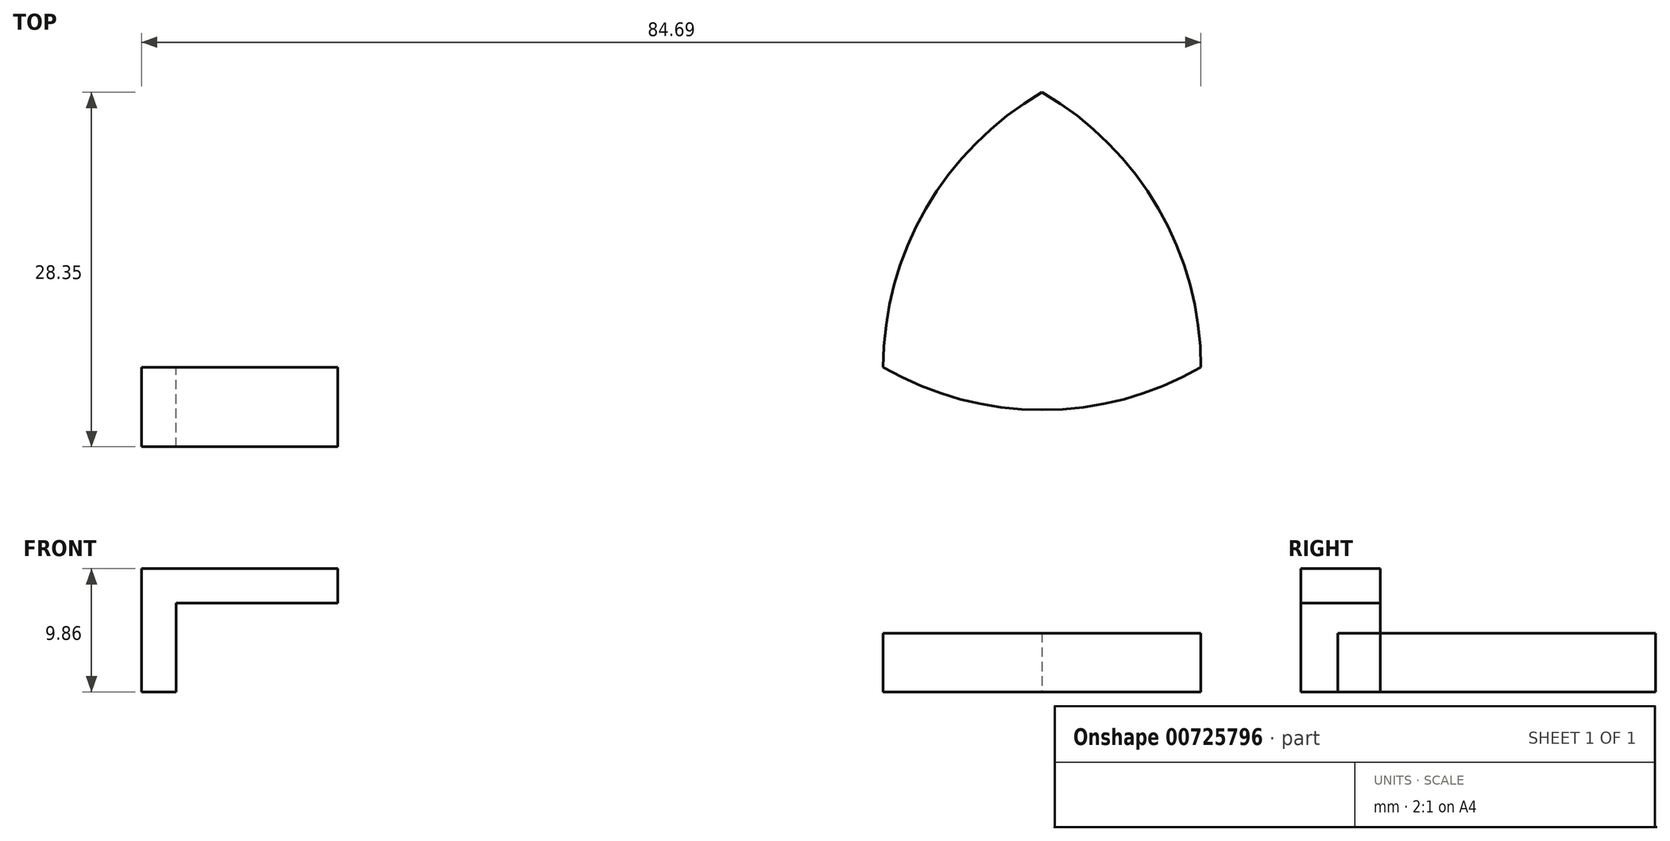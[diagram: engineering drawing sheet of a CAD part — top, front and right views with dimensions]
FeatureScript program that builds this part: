
annotation { "Feature Type Name" : "Feature", "Feature Type Description" : "" }
export const myFeature = defineFeature(function(context is Context, id is Id, definition is map)
    precondition{}
    {
        {
            var Q0;
            Q0=qCreatedBy(makeId("Top.planeOp"),FACE);
            var sketch = newSketch(context, id + "F0", { "sketchPlane" : qUnion([Q0])});
            skArc(sketch, "E0", {"start": v(-12.7, 0) * mm, "mid": v(0, -3.4) * mm, "end": v(12.7, 0) * mm});
            skArc(sketch, "E1", {"start": v(0, 22) * mm, "mid": v(-9.3, 12.7) * mm, "end": v(-12.7, 0) * mm});
            skArc(sketch, "E2", {"start": v(12.7, 0) * mm, "mid": v(9.3, 12.7) * mm, "end": v(0, 22) * mm});
            skPoint(sketch, "E3.end.orphan", {"position": v(6.35, 11) * mm});
            skPoint(sketch, "E4.end.orphan", {"position": v(-6.35, 11) * mm});
            skSolve(sketch);
        }
        {
            var Q0;
            Q0 = qSketchRegion(id + "F0", true);
            extrude(context, id + "F1", {"entities" : qUnion([Q0]), "depth" : 4.7 * mm, "offsetDistance" : 25.4 * mm});
        }
        {
            var Q0;
            Q0=qCreatedBy(makeId("Front.planeOp"),FACE);
            var sketch = newSketch(context, id + "F2", { "sketchPlane" : qUnion([Q0])});
            skLineSegment(sketch, "E5.bottom", {"start": v(-72, 0) * mm, "end": v(-69.23, 0) * mm});
            skLineSegment(sketch, "E5.top", {"start": v(-72, 7.1) * mm, "end": v(-69.23, 7.1) * mm});
            skLineSegment(sketch, "E5.left", {"start": v(-72, 0) * mm, "end": v(-72, 7.1) * mm});
            skLineSegment(sketch, "E5.right", {"start": v(-69.23, 0) * mm, "end": v(-69.23, 7.1) * mm});
            skLineSegment(sketch, "E6.bottom", {"start": v(-72, 7.1) * mm, "end": v(-56.32, 7.1) * mm});
            skLineSegment(sketch, "E6.top", {"start": v(-72, 9.86) * mm, "end": v(-56.32, 9.86) * mm});
            skLineSegment(sketch, "E6.left", {"start": v(-72, 7.1) * mm, "end": v(-72, 9.86) * mm});
            skLineSegment(sketch, "E6.right", {"start": v(-56.32, 7.1) * mm, "end": v(-56.32, 9.86) * mm});
            skLineSegment(sketch, "E7.bottom", {"start": v(-56.32, 7.1) * mm, "end": v(-58.72, 7.1) * mm});
            skLineSegment(sketch, "E7.top", {"start": v(-56.32, 0) * mm, "end": v(-58.72, 0) * mm});
            skLineSegment(sketch, "E7.left", {"start": v(-56.32, 7.1) * mm, "end": v(-56.32, 0) * mm});
            skLineSegment(sketch, "E7.right", {"start": v(-58.72, 7.1) * mm, "end": v(-58.72, 0) * mm});
            skSolve(sketch);
        }
        {
            var Q0;
            Q0=makeQuery(id+"F2.imprint","IMPRINT",FACE,{"disambiguationData":[TD([[makeQuery(id+"F2.imprint","IMPRINT",EDGE,{"derivedFrom":sQuery(id+"F2.wireOp",EDGE,"E5.bottom")}),1.0]])]});
            var Q1;
            Q1=makeQuery(id+"F2.imprint","IMPRINT",FACE,{"disambiguationData":[TD([[makeQuery(id+"F2.imprint","IMPRINT",EDGE,{"derivedFrom":sQuery(id+"F2.wireOp",EDGE,"E6.top")}),-1.0]])]});
            var Q2;
            Q2=makeQuery(id+"F2.imprint","IMPRINT",FACE,{"disambiguationData":[TD([[makeQuery(id+"F2.imprint","IMPRINT",EDGE,{"derivedFrom":sQuery(id+"F2.wireOp",EDGE,"E7.bottom")}),1.0]])]});
            extrude(context, id + "F3", {"entities" : qUnion([Q0, Q1, Q2]), "depth" : 6.35 * mm, "offsetDistance" : 25.4 * mm});
        }
    });
